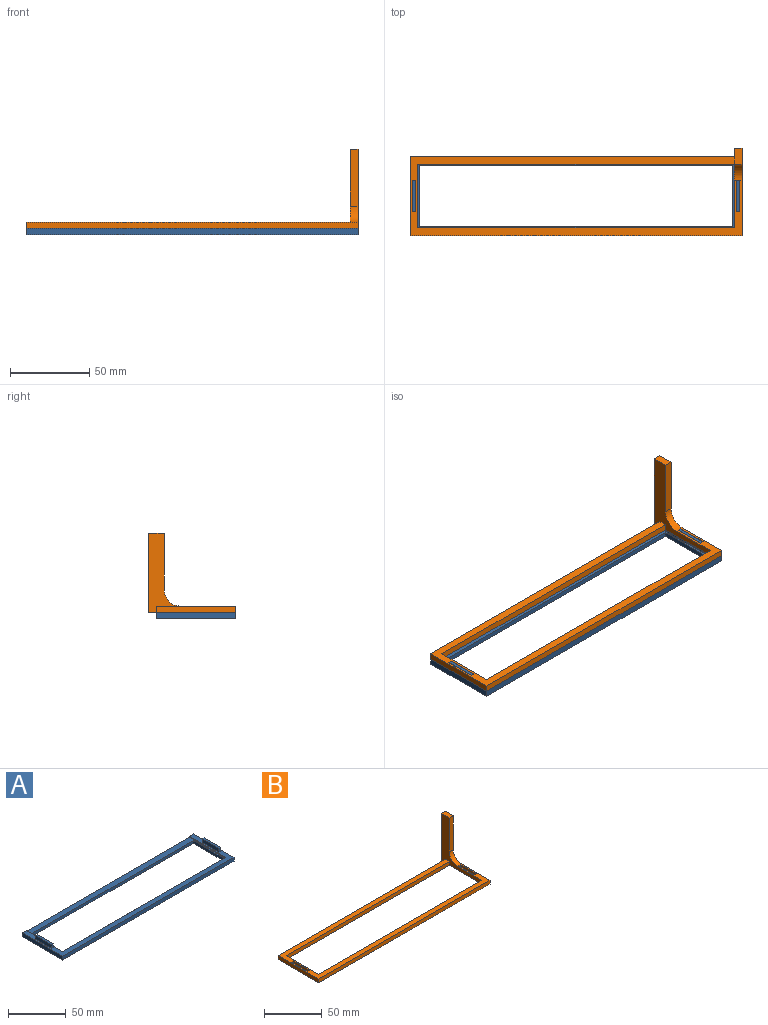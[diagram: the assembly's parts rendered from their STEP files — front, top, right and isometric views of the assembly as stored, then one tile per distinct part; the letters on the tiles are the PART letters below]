
ASSEMBLY  parts=2 mates=1
PART A: 24 faces, bbox 210x50x8 mm
  f0: plane 210x50mm, normal (0,0,1), area 1420.1mm2, adj f1,f7,f8,f9,f10,f11,f13,f14
  f1: plane 210x4mm, normal (0,1,0), area 640mm2, adj f0,f6,f7,f8,f10,f11,f12
  f2: plane 38x3mm, normal (-1,0,0), area 114mm2, adj f3,f5,f6,f12
  f3: plane 198x3mm, normal (0,-1,0), area 594mm2, adj f2,f4,f6,f12
  f4: plane 38x3mm, normal (1,0,0), area 114mm2, adj f3,f5,f6,f12
  f5: plane 198x3mm, normal (0,1,0), area 594mm2, adj f2,f4,f6,f12
  f6: plane 210x50mm, normal (0,0,-1), area 2976mm2, adj f1,f2,f3,f4,f5,f7,f8,f9
  f7: plane 50x4mm, normal (1,0,0), area 200mm2, adj f0,f1,f6,f9
  f8: plane 50x4mm, normal (-1,0,0), area 200mm2, adj f0,f1,f6,f9
  f9: plane 210x4mm, normal (0,-1,0), area 840mm2, adj f0,f6,f7,f8
  f10: plane 45x1mm, normal (-1,0,0), area 45mm2, adj f0,f1,f12,f13
  f11: plane 45x1mm, normal (1,0,0), area 45mm2, adj f0,f1,f12,f13
  f12: plane 200x45mm, normal (0,0,1), area 1476mm2, adj f1,f2,f3,f4,f5,f10,f11,f13
  f13: plane 200x1mm, normal (0,1,0), area 200mm2, adj f0,f10,f11,f12
  f14: plane 4x2mm, normal (0,1,0), area 8mm2, adj f0,f15,f17,f18
  f15: plane 19.97x4mm, normal (-1,0,0), area 79.9mm2, adj f0,f14,f16,f18
  f16: plane 4x2mm, normal (0,-1,0), area 8mm2, adj f0,f15,f17,f18
  f17: plane 19.97x4mm, normal (1,0,0), area 79.9mm2, adj f0,f14,f16,f18
  f18: plane 19.97x2mm, normal (0,0,1), area 39.9mm2, adj f14,f15,f16,f17
  f19: plane 4x2mm, normal (0,1,0), area 8mm2, adj f0,f20,f22,f23
  f20: plane 19.97x4mm, normal (-1,0,0), area 79.9mm2, adj f0,f19,f21,f23
  f21: plane 4x2mm, normal (0,-1,0), area 8mm2, adj f0,f20,f22,f23
  f22: plane 19.97x4mm, normal (1,0,0), area 79.9mm2, adj f0,f19,f21,f23
  f23: plane 19.97x2mm, normal (0,0,1), area 39.9mm2, adj f19,f20,f21,f22
PART B: 22 faces, bbox 210x55x50 mm
  f0: plane 205x4mm, normal (0,1,0), area 820mm2, adj f1,f2,f4,f7
  f1: plane 210x50mm, normal (0,0,1), area 2329mm2, adj f0,f3,f4,f5,f6,f7,f8,f9
  f2: plane 210x55mm, normal (0,0,-1), area 2429mm2, adj f0,f3,f4,f5,f6,f7,f8,f9
  f3: plane 200x4mm, normal (0,-1,0), area 800mm2, adj f1,f2,f4,f9
  f4: plane 50x50mm, normal (-1,0,0), area 661.5mm2, adj f0,f1,f2,f3,f5,f18,f19,f20
  f5: plane 200x4mm, normal (0,1,0), area 800mm2, adj f1,f2,f4,f9
  f6: plane 55x50mm, normal (1,0,0), area 701.5mm2, adj f1,f2,f8,f18,f19,f20,f21
  f7: plane 50x4mm, normal (-1,0,0), area 200mm2, adj f0,f1,f2,f8
  f8: plane 210x4mm, normal (0,-1,0), area 840mm2, adj f1,f2,f6,f7
  f9: plane 40x4mm, normal (1,0,0), area 160mm2, adj f1,f2,f3,f5
  f10: plane 4x2.4mm, normal (0,-1,0), area 9.6mm2, adj f2,f11,f13,f21
  f11: plane 20x4mm, normal (1,0,0), area 80mm2, adj f1,f2,f10,f12
  f12: plane 4x2.4mm, normal (0,1,0), area 9.6mm2, adj f1,f2,f11,f13
  f13: plane 20x4mm, normal (-1,0,0), area 80mm2, adj f1,f2,f10,f12
  f14: plane 4x2.4mm, normal (0,-1,0), area 9.6mm2, adj f1,f2,f15,f17
  f15: plane 20x4mm, normal (1,0,0), area 80mm2, adj f1,f2,f14,f16
  f16: plane 4x2.4mm, normal (0,1,0), area 9.6mm2, adj f1,f2,f15,f17
  f17: plane 20x4mm, normal (-1,0,0), area 80mm2, adj f1,f2,f14,f16
  f18: plane 36x5mm, normal (0,-1,0), area 180mm2, adj f4,f6,f20,f21
  f19: plane 50x5mm, normal (0,1,0), area 250mm2, adj f2,f4,f6,f20
  f20: plane 10x5mm, normal (0,0,1), area 50mm2, adj f4,f6,f18,f19
  f21: cylinder r=10mm len=10mm, axis (1,0,0), area 78.5mm2, adj f1,f4,f6,f10,f18
PLACE A t=(105,25,0)mm
PLACE B t=(105,25,4)mm
MATE planar B.f2 <-> A.f0  axis (0,0,-1) through (5,5,4)mm
